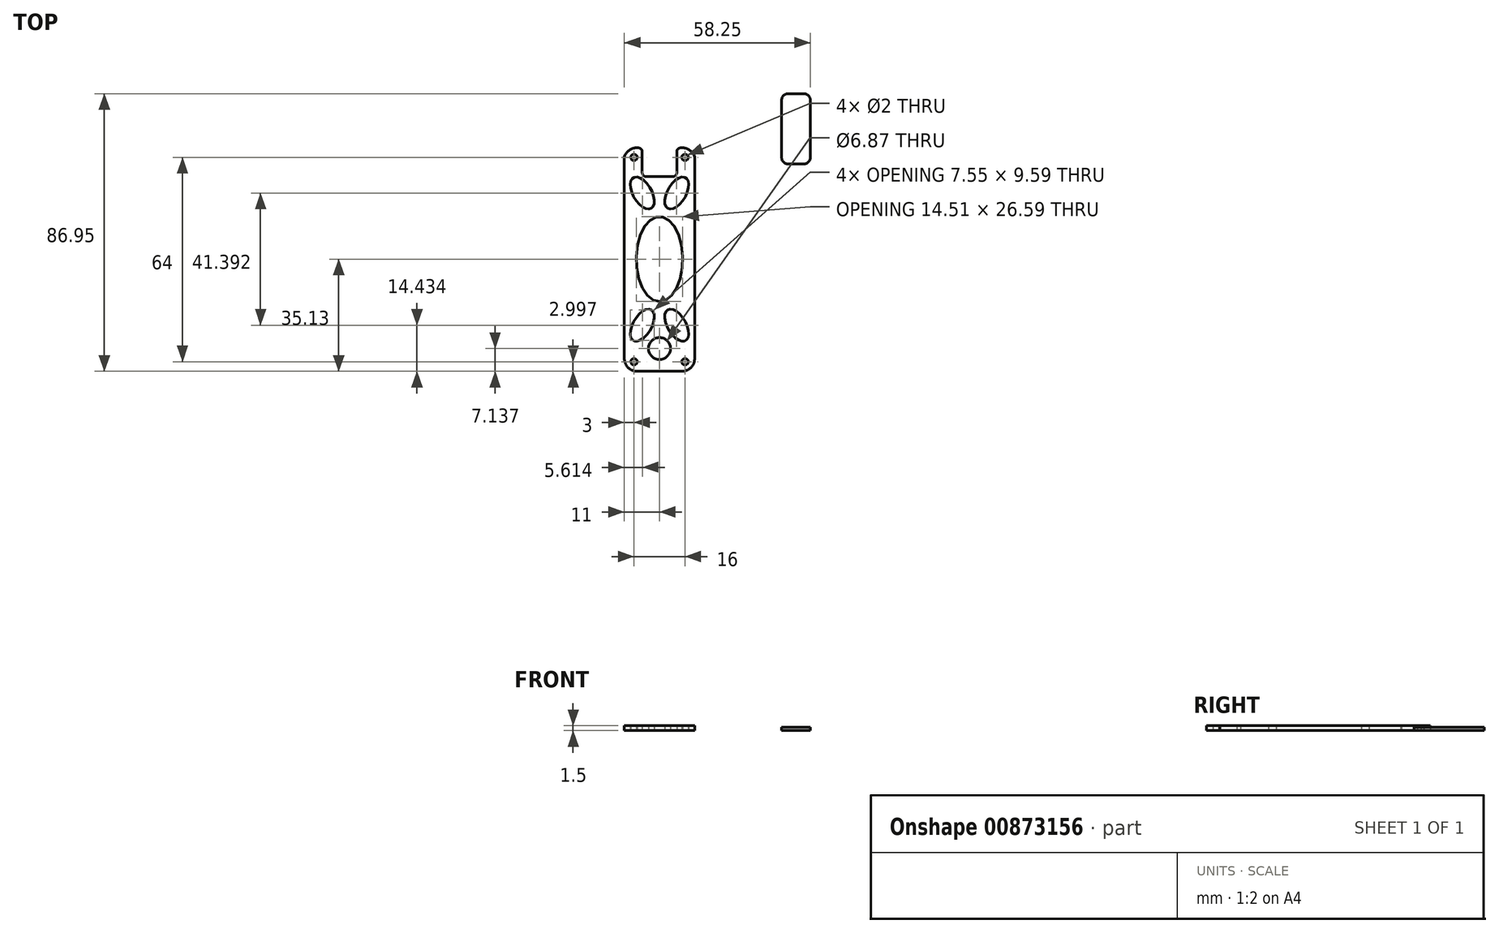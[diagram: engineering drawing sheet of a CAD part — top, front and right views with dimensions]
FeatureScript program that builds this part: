
annotation { "Feature Type Name" : "Feature", "Feature Type Description" : "" }
export const myFeature = defineFeature(function(context is Context, id is Id, definition is map)
    precondition{}
    {
        {
            var Q0;
            Q0=qCreatedBy(makeId("Top.planeOp"),FACE);
            var sketch = newSketch(context, id + "F0", { "sketchPlane" : qUnion([Q0])});
            skCircle(sketch, "E0", {"center": v(-8, 31.87) * mm, "radius": 1 * mm});
            skCircle(sketch, "E1.MirrorC", {"center": v(8, 31.87) * mm, "radius": 1 * mm});
            skCircle(sketch, "E2.MirrorC", {"center": v(-8, -32.13) * mm, "radius": 1 * mm});
            skCircle(sketch, "E3.MirrorC", {"center": v(8, -32.13) * mm, "radius": 1 * mm});
            skArc(sketch, "E4", {"start": v(-7.23, 34.87) * mm, "mid": v(-9.59, 34.05) * mm, "end": v(-11, 32) * mm});
            skLineSegment(sketch, "E5", {"start": v(-11, 32) * mm, "end": v(-11, -30) * mm});
            skLineSegment(sketch, "E6", {"start": v(11, -30) * mm, "end": v(11, 32) * mm});
            skLineSegment(sketch, "E7", {"start": v(-7.17, -35.13) * mm, "end": v(6.83, -35.13) * mm});
            skLineSegment(sketch, "E8", {"start": v(-5.42, 28.85) * mm, "end": v(-5.42, 27.12) * mm});
            skEllipse(sketch, "E9", {"center": v(0, 0) * mm, "majorRadius": 13.3 * mm, "minorRadius": 7.26 * mm, "majorAxis": v(0, -1)});
            skEllipse(sketch, "E10", {"center": v(-5.39, 20.7) * mm, "majorRadius": 5.57 * mm, "minorRadius": 2.91 * mm, "majorAxis": v(0.5, -0.86)});
            skPoint(sketch, "E10.centerSnap0", {"position": v(-7.4, 20.7) * mm});
            skEllipse(sketch, "E11.MirrorC", {"center": v(5.39, 20.7) * mm, "majorRadius": 5.57 * mm, "minorRadius": 2.91 * mm, "majorAxis": v(-0.5, -0.86)});
            skEllipse(sketch, "E12.MirrorC", {"center": v(5.39, -20.7) * mm, "majorRadius": 5.57 * mm, "minorRadius": 2.91 * mm, "majorAxis": v(-0.5, 0.86)});
            skEllipse(sketch, "E13.MirrorC", {"center": v(-5.39, -20.7) * mm, "majorRadius": 5.57 * mm, "minorRadius": 2.91 * mm, "majorAxis": v(0.5, 0.86)});
            skCircle(sketch, "E14", {"center": v(0, -28) * mm, "radius": 3.44 * mm});
            skArc(sketch, "E15.MirrorCS", {"start": v(7.23, 34.87) * mm, "mid": v(9.59, 34.05) * mm, "end": v(11, 32) * mm});
            skLineSegment(sketch, "E16", {"start": v(-7.23, 34.87) * mm, "end": v(-6.67, 34.87) * mm});
            skLineSegment(sketch, "E17", {"start": v(-5.42, 28.85) * mm, "end": v(-5.42, 33.62) * mm});
            skArc(sketch, "E18.filletArc", {"start": v(-5.42, 27.12) * mm, "mid": v(-5.05, 26.23) * mm, "end": v(-4.17, 25.87) * mm});
            skArc(sketch, "E19.filletArc", {"start": v(-5.42, 33.62) * mm, "mid": v(-5.79, 34.5) * mm, "end": v(-6.67, 34.87) * mm});
            skArc(sketch, "E20.MirrorCS", {"start": v(5.42, 33.62) * mm, "mid": v(5.79, 34.5) * mm, "end": v(6.67, 34.87) * mm});
            skArc(sketch, "E21.MirrorCS", {"start": v(5.42, 27.12) * mm, "mid": v(5.05, 26.23) * mm, "end": v(4.17, 25.87) * mm});
            skLineSegment(sketch, "E22", {"start": v(6.67, 34.87) * mm, "end": v(7.23, 34.87) * mm});
            skLineSegment(sketch, "E23", {"start": v(-4.17, 25.87) * mm, "end": v(4.17, 25.87) * mm});
            skLineSegment(sketch, "E24", {"start": v(5.42, 33.62) * mm, "end": v(5.42, 28.85) * mm});
            skLineSegment(sketch, "E25", {"start": v(5.42, 28.85) * mm, "end": v(5.42, 27.12) * mm});
            skLineSegment(sketch, "E26.bottom", {"start": v(-7, -35.13) * mm, "end": v(7, -35.13) * mm});
            skPoint(sketch, "E27.visualSharp", {"position": v(-11, -35.13) * mm});
            skArc(sketch, "E27.filletArc", {"start": v(-11, -31) * mm, "mid": v(-9.88, -33.92) * mm, "end": v(-7, -35.13) * mm});
            skPoint(sketch, "E28.visualSharp", {"position": v(11, -35.13) * mm});
            skArc(sketch, "E28.filletArc", {"start": v(7, -35.13) * mm, "mid": v(9.88, -33.92) * mm, "end": v(11, -31) * mm});
            skLineSegment(sketch, "E29", {"start": v(-11, -30) * mm, "end": v(-11, -31) * mm});
            skLineSegment(sketch, "E30", {"start": v(11, -30) * mm, "end": v(11, -31) * mm});
            skLineSegment(sketch, "E31", {"start": v(11, -31) * mm, "end": v(11, 37.12) * mm});
            skSolve(sketch);
        }
        {
            var Q0;
            Q0=makeQuery(id+"F0.imprint","IMPRINT",FACE,{"disambiguationData":[TD([[makeQuery(id+"F0.imprint","IMPRINT",EDGE,{"derivedFrom":sQuery(id+"F0.wireOp",EDGE,"E0")}),-1.0]])]});
            extrude(context, id + "F1", {"entities" : qUnion([Q0]), "depth" : 1.5 * mm, "offsetDistance" : 25 * mm});
        }
        {
            var Q0;
            Q0=qCreatedBy(makeId("Top.planeOp"),FACE);
            var sketch = newSketch(context, id + "F2", { "sketchPlane" : qUnion([Q0])});
            skLineSegment(sketch, "E32.bottom", {"start": v(40.25, 51.82) * mm, "end": v(45.25, 51.82) * mm});
            skLineSegment(sketch, "E32.top", {"start": v(40.25, 29.82) * mm, "end": v(45.25, 29.82) * mm});
            skLineSegment(sketch, "E32.left", {"start": v(38.25, 49.82) * mm, "end": v(38.25, 31.82) * mm});
            skLineSegment(sketch, "E32.right", {"start": v(47.25, 49.82) * mm, "end": v(47.25, 31.82) * mm});
            skPoint(sketch, "E33.visualSharp", {"position": v(38.25, 51.82) * mm});
            skArc(sketch, "E33.filletArc", {"start": v(40.25, 51.82) * mm, "mid": v(38.84, 51.23) * mm, "end": v(38.25, 49.82) * mm});
            skPoint(sketch, "E34.visualSharp", {"position": v(47.25, 51.82) * mm});
            skArc(sketch, "E34.filletArc", {"start": v(47.25, 49.82) * mm, "mid": v(46.66, 51.23) * mm, "end": v(45.25, 51.82) * mm});
            skPoint(sketch, "E35.visualSharp", {"position": v(38.25, 29.82) * mm});
            skArc(sketch, "E35.filletArc", {"start": v(38.25, 31.82) * mm, "mid": v(38.84, 30.4) * mm, "end": v(40.25, 29.82) * mm});
            skPoint(sketch, "E36.visualSharp", {"position": v(47.25, 29.82) * mm});
            skArc(sketch, "E36.filletArc", {"start": v(45.25, 29.82) * mm, "mid": v(46.66, 30.4) * mm, "end": v(47.25, 31.82) * mm});
            skSolve(sketch);
        }
        {
            var Q0;
            Q0=makeQuery(id+"F2.imprint","IMPRINT",FACE,{"disambiguationData":[TD([[makeQuery(id+"F2.imprint","IMPRINT",EDGE,{"derivedFrom":sQuery(id+"F2.wireOp",EDGE,"E32.bottom")}),-1.0]])]});
            extrude(context, id + "F3", {"entities" : qUnion([Q0]), "depth" : 1 * mm, "offsetDistance" : 25 * mm});
        }
    });
